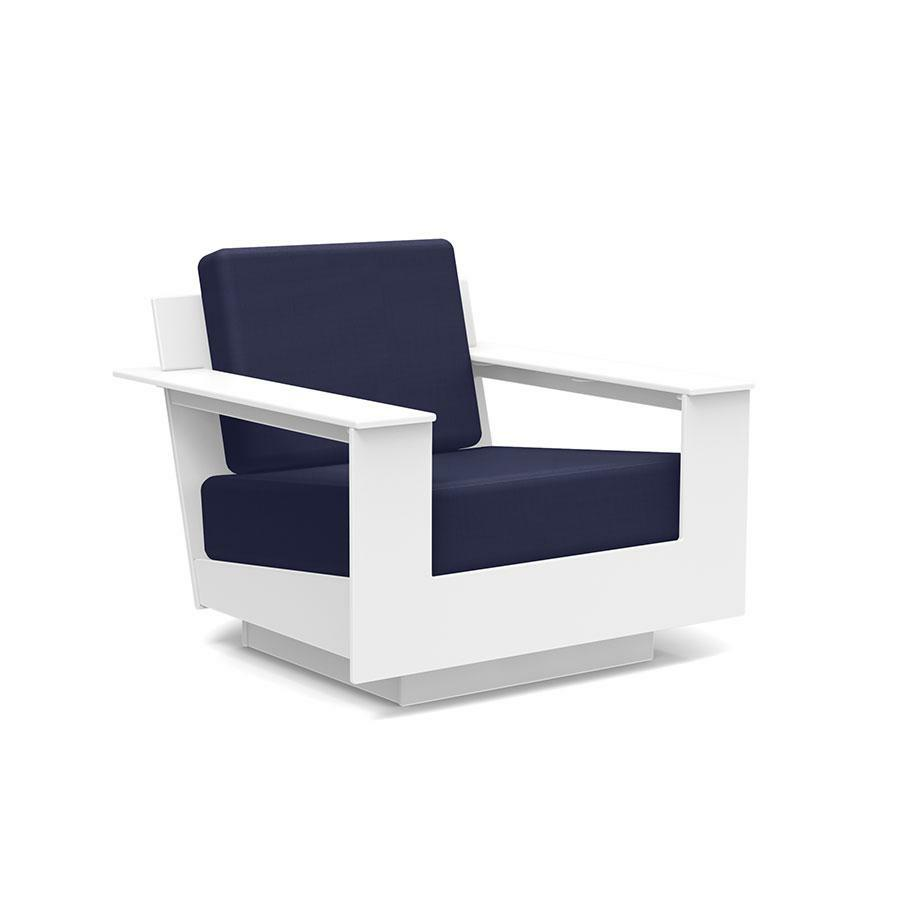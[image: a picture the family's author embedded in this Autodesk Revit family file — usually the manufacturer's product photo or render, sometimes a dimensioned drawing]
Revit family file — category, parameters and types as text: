
# Revit family: Lollygagger Nisswa Lounge Chair
name_source: partatom
category: Furniture
revit_build: Autodesk Revit 2016 (Build: 20150220_1215(x64)
units: mm (PartAtom-declared; Revit-internal decimal feet)

## family parameters
Always vertical = No
Cut with Voids When Loaded = No
OmniClass Number = 23.40.20.00
OmniClass Title = General Furniture and Specialties
Room Calculation Point = No
Shared = No
Work Plane-Based = No

## types (10) — shared parameters
Height = 28 1/8"
Length = 33"
Manufacturer = Loll
Thick = 1/2"
Type Image = Nisswa Lounge Chair.jpg
URL = https://lolldesigns.com
Width = 31 19/32"

## per-type parameters (varying)
| type | Finish Material |
| Loll-Black | Loll-White |
| Loll-Sunset | Loll-Sunset |
| Loll-Chocolate | Loll-Chocolate |
| Loll-Sky | Loll-Sky |
| Loll-Apple | Loll-Apple |
| Loll-Leaf | Loll-Leaf |
| Loll-Charcoal | Loll-Charcoal |
| Loll-Navy Blue | Loll-Navy Blue |
| Loll-White | Loll-White |
| Loll-Driftwood | Loll-Driftwood |

## geometry (parser evidence)
native form markers: Blend x4, Sweep x17
no freeform markers — native parametric forms only
